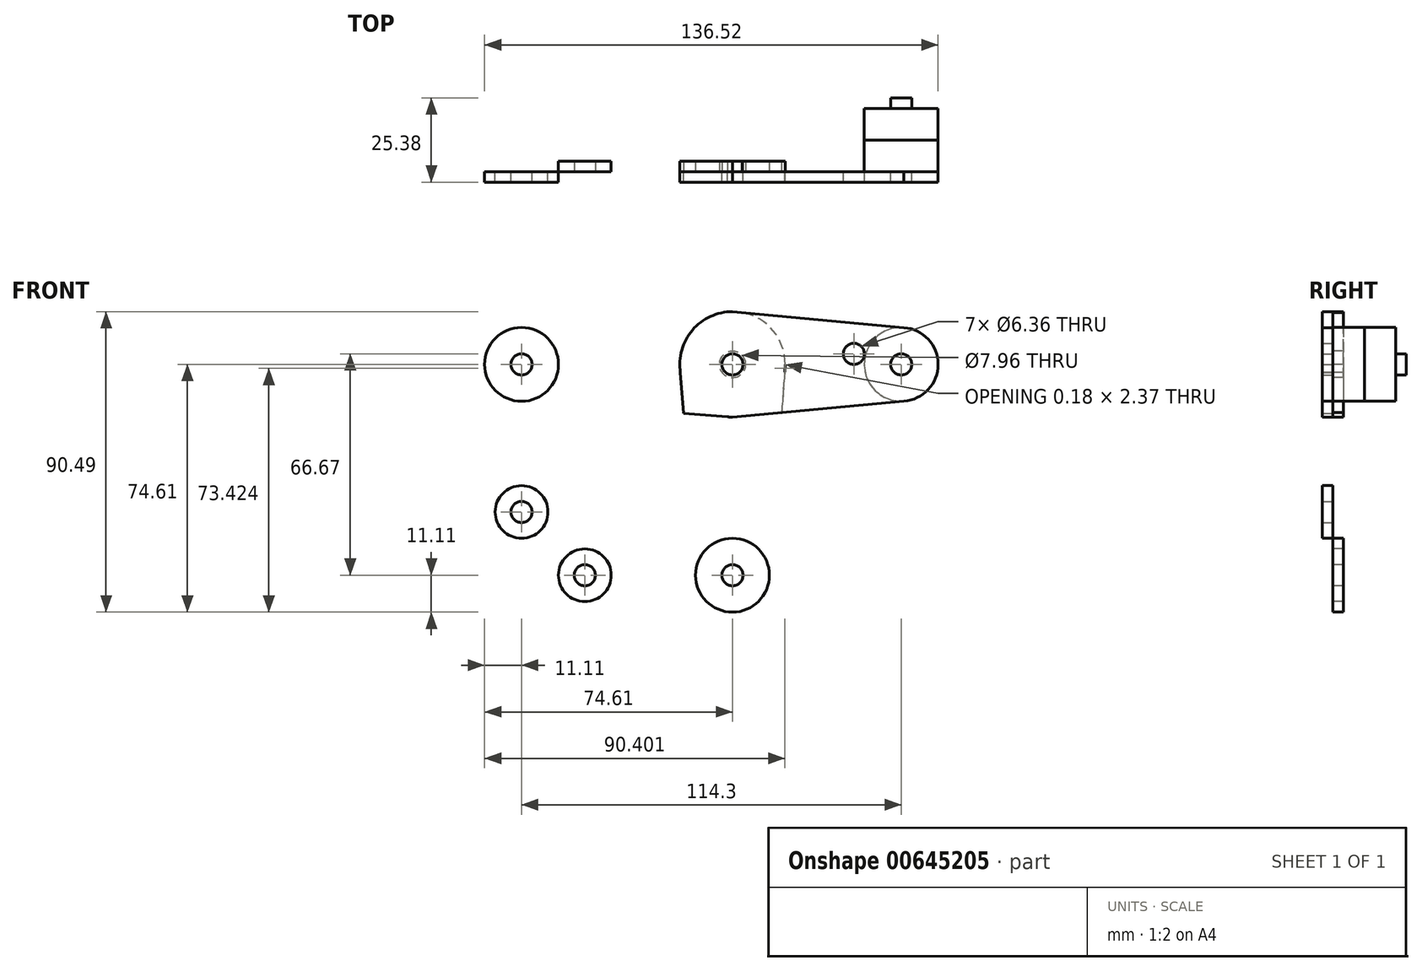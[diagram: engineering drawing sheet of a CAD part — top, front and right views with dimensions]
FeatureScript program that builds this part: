
annotation { "Feature Type Name" : "Feature", "Feature Type Description" : "" }
export const myFeature = defineFeature(function(context is Context, id is Id, definition is map)
    precondition{}
    {
        {
            var Q0;
            Q0=qCreatedBy(makeId("Front.planeOp"),FACE);
            var sketch = newSketch(context, id + "F0", { "sketchPlane" : qUnion([Q0])});
            skCircle(sketch, "E0", {"center": v(0, 0) * mm, "radius": 3.98 * mm});
            skCircle(sketch, "E1", {"center": v(0, 0) * mm, "radius": 15.88 * mm});
            skCircle(sketch, "E2", {"center": v(50.8, 0) * mm, "radius": 11.11 * mm});
            skCircle(sketch, "E3", {"center": v(50.8, 0) * mm, "radius": 3.18 * mm});
            skLineSegment(sketch, "E4", {"start": v(0, -15.88) * mm, "end": v(51.83, -11.06) * mm});
            skLineSegment(sketch, "E5", {"start": v(0, 15.88) * mm, "end": v(51.83, 11.06) * mm});
            skCircle(sketch, "E6", {"center": v(36.53, 3.17) * mm, "radius": 3.18 * mm});
            skLineSegment(sketch, "E7", {"start": v(0, 0) * mm, "end": v(50.8, 0) * mm, "construction": true});
            skCircle(sketch, "E8", {"center": v(-63.5, 0) * mm, "radius": 11.11 * mm});
            skLineSegment(sketch, "E9", {"start": v(-63.5, 0) * mm, "end": v(0, 0) * mm, "construction": true});
            skCircle(sketch, "E10", {"center": v(-63.5, 0) * mm, "radius": 3.18 * mm});
            skCircle(sketch, "E11", {"center": v(-63.5, -44.45) * mm, "radius": 7.94 * mm});
            skCircle(sketch, "E12", {"center": v(-63.5, -44.45) * mm, "radius": 3.18 * mm});
            skLineSegment(sketch, "E13", {"start": v(-63.5, 0) * mm, "end": v(-63.5, -44.45) * mm, "construction": true});
            skCircle(sketch, "E14", {"center": v(0, -63.5) * mm, "radius": 3.18 * mm});
            skCircle(sketch, "E15", {"center": v(0, -63.5) * mm, "radius": 11.11 * mm});
            skCircle(sketch, "E16", {"center": v(0, -42.85) * mm, "radius": 3.18 * mm});
            skLineSegment(sketch, "E17", {"start": v(0, 0) * mm, "end": v(0, -63.5) * mm, "construction": true});
            skCircle(sketch, "E18", {"center": v(-44.45, -63.5) * mm, "radius": 7.94 * mm});
            skLineSegment(sketch, "E19", {"start": v(0, -63.5) * mm, "end": v(-44.45, -63.5) * mm, "construction": true});
            skCircle(sketch, "E20", {"center": v(-44.45, -63.5) * mm, "radius": 3.18 * mm});
            skLineSegment(sketch, "E21", {"start": v(-63.5, -44.45) * mm, "end": v(-44.45, -63.5) * mm, "construction": true});
            skLineSegment(sketch, "E22", {"start": v(-44.45, -71.44) * mm, "end": v(0, -74.64) * mm});
            skLineSegment(sketch, "E23", {"start": v(-15.87, 0) * mm, "end": v(-12.5, -45.27) * mm});
            skLineSegment(sketch, "E24", {"start": v(-44.45, -55.56) * mm, "end": v(-19.86, -53.8) * mm});
            skPoint(sketch, "E25.newPointB", {"position": v(0, -52.36) * mm});
            skArc(sketch, "E25.filletArc", {"start": v(-19.86, -53.8) * mm, "mid": v(-14.41, -51.06) * mm, "end": v(-12.5, -45.27) * mm});
            skLineSegment(sketch, "E26", {"start": v(15.88, 0) * mm, "end": v(11.11, -63.5) * mm});
            skCircle(sketch, "E27", {"center": v(0, 0) * mm, "radius": 3.18 * mm});
            skLineSegment(sketch, "E28", {"start": v(-64.33, 11.08) * mm, "end": v(-1.2, 15.83) * mm});
            skLineSegment(sketch, "E29", {"start": v(-74.58, -0.8) * mm, "end": v(-71.42, -45.02) * mm});
            skLineSegment(sketch, "E30", {"start": v(-53.78, -19.88) * mm, "end": v(-55.58, -45.02) * mm});
            skLineSegment(sketch, "E31", {"start": v(-45.26, -12.52) * mm, "end": v(-1.2, -15.83) * mm});
            skPoint(sketch, "E32.newPointB", {"position": v(-52.36, 0) * mm});
            skArc(sketch, "E32.filletArc", {"start": v(-45.26, -12.52) * mm, "mid": v(-51.05, -14.43) * mm, "end": v(-53.78, -19.88) * mm});
            skSolve(sketch);
        }
        {
            var Q0;
            {var subQ0=sQuery(id+"F0.wireOp",EDGE,"E28");Q0=makeQuery(id+"F0.imprint","IMPRINT",FACE,{"disambiguationData":[TD([[makeQuery(id+"F0.imprint","IMPRINT",EDGE,{"derivedFrom":subQ0}),-1.0]])]});}
            var Q1;
            Q1=makeQuery(id+"F0.imprint","IMPRINT",FACE,{"disambiguationData":[TD([[makeQuery(id+"F0.imprint","IMPRINT",EDGE,{"derivedFrom":sQuery(id+"F0.wireOp",EDGE,"E6")}),-1.0]])]});
            var Q2;
            Q2=makeQuery(id+"F0.imprint","IMPRINT",FACE,{"disambiguationData":[TD([[makeQuery(id+"F0.imprint","IMPRINT",EDGE,{"derivedFrom":sQuery(id+"F0.wireOp",EDGE,"E0")}),-1.0]])]});
            var Q3;
            {var subQ0=sQuery(id+"F0.wireOp",EDGE,"E31");var subQ1=sQuery(id+"F0.wireOp",EDGE,"E1");var subQ2=makeQuery(id+"F0.imprint","INTERSECT",VERTEX,{"derivedFrom":[subQ1,subQ0]});Q3=makeQuery(id+"F0.imprint","IMPRINT",FACE,{"disambiguationData":[TD([[makeQuery(id+"F0.imprint","IMPRINT",EDGE,{"disambiguationData":[TD([[subQ2,1.0]])],"derivedFrom":subQ1}),-1.0]])]});}
            var Q4;
            {var subQ0=sQuery(id+"F0.wireOp",EDGE,"E4");var subQ1=sQuery(id+"F0.wireOp",EDGE,"E1");var subQ2=makeQuery(id+"F0.imprint","INTERSECT",VERTEX,{"disambiguationData":[OD(1.0)],"derivedFrom":[subQ1,subQ0]});Q4=makeQuery(id+"F0.imprint","IMPRINT",FACE,{"disambiguationData":[TD([[makeQuery(id+"F0.imprint","IMPRINT",EDGE,{"disambiguationData":[TD([[subQ2,-1.0]])],"derivedFrom":subQ1}),-1.0]])]});}
            var Q5;
            Q5=makeQuery(id+"F0.imprint","IMPRINT",FACE,{"disambiguationData":[TD([[makeQuery(id+"F0.imprint","IMPRINT",EDGE,{"derivedFrom":sQuery(id+"F0.wireOp",EDGE,"E3")}),-1.0]])]});
            var Q6;
            Q6=makeQuery(id+"F0.imprint","IMPRINT",FACE,{"disambiguationData":[TD([[makeQuery(id+"F0.imprint","IMPRINT",EDGE,{"derivedFrom":sQuery(id+"F0.wireOp",EDGE,"E10")}),-1.0]])]});
            var Q7;
            Q7=makeQuery(id+"F0.imprint","IMPRINT",FACE,{"disambiguationData":[TD([[makeQuery(id+"F0.imprint","IMPRINT",EDGE,{"derivedFrom":sQuery(id+"F0.wireOp",EDGE,"E12")}),-1.0]])]});
            var Q8;
            Q8=makeQuery(id+"F0.imprint","IMPRINT",FACE,{"disambiguationData":[TD([[makeQuery(id+"F0.imprint","IMPRINT",EDGE,{"derivedFrom":sQuery(id+"F0.wireOp",EDGE,"E0")}),1.0]])]});
            extrude(context, id + "F1", {"entities" : qUnion([Q0, Q1, Q2, Q3, Q4, Q5, Q6, Q7, Q8]), "depth" : 3.17 * mm, "offsetDistance" : 25.4 * mm});
        }
        {
            var Q0;
            {var subQ0=sQuery(id+"F0.wireOp",EDGE,"E31");var subQ1=sQuery(id+"F0.wireOp",EDGE,"E1");var subQ2=makeQuery(id+"F0.imprint","INTERSECT",VERTEX,{"derivedFrom":[subQ1,subQ0]});Q0=makeQuery(id+"F0.imprint","IMPRINT",FACE,{"disambiguationData":[TD([[makeQuery(id+"F0.imprint","IMPRINT",EDGE,{"disambiguationData":[TD([[subQ2,1.0]])],"derivedFrom":subQ1}),-1.0]])]});}
            var Q1;
            {var subQ0=sQuery(id+"F0.wireOp",EDGE,"E4");var subQ1=sQuery(id+"F0.wireOp",EDGE,"E1");var subQ2=makeQuery(id+"F0.imprint","INTERSECT",VERTEX,{"disambiguationData":[OD(1.0)],"derivedFrom":[subQ1,subQ0]});Q1=makeQuery(id+"F0.imprint","IMPRINT",FACE,{"disambiguationData":[TD([[makeQuery(id+"F0.imprint","IMPRINT",EDGE,{"disambiguationData":[TD([[subQ2,-1.0]])],"derivedFrom":subQ1}),-1.0]])]});}
            var Q2;
            Q2=makeQuery(id+"F0.imprint","IMPRINT",FACE,{"disambiguationData":[TD([[makeQuery(id+"F0.imprint","IMPRINT",EDGE,{"derivedFrom":sQuery(id+"F0.wireOp",EDGE,"E0")}),-1.0]])]});
            var Q3;
            Q3=makeQuery(id+"F0.imprint","IMPRINT",FACE,{"disambiguationData":[TD([[makeQuery(id+"F0.imprint","IMPRINT",EDGE,{"derivedFrom":sQuery(id+"F0.wireOp",EDGE,"E16")}),-1.0]])]});
            var Q4;
            Q4=makeQuery(id+"F0.imprint","IMPRINT",FACE,{"disambiguationData":[TD([[makeQuery(id+"F0.imprint","IMPRINT",EDGE,{"derivedFrom":sQuery(id+"F0.wireOp",EDGE,"E14")}),-1.0]])]});
            var Q5;
            Q5=makeQuery(id+"F0.imprint","IMPRINT",FACE,{"disambiguationData":[TD([[makeQuery(id+"F0.imprint","IMPRINT",EDGE,{"derivedFrom":sQuery(id+"F0.wireOp",EDGE,"E20")}),-1.0]])]});
            extrude(context, id + "F2", {"entities" : qUnion([Q0, Q1, Q2, Q3, Q4, Q5]), "oppositeDirection" : true, "depth" : 3.17 * mm, "offsetDistance" : 25.4 * mm});
        }
        {
            var Q0;
            Q0=makeQuery(id+"F1.opExtrude","CAP_FACE",FACE,{"disambiguationData":[OSD([sQuery(id+"F0.wireOp",EDGE,"E0"),sQuery(id+"F0.wireOp",EDGE,"E1"),sQuery(id+"F0.wireOp",EDGE,"E2"),sQuery(id+"F0.wireOp",EDGE,"E3"),sQuery(id+"F0.wireOp",EDGE,"E4"),sQuery(id+"F0.wireOp",EDGE,"E5"),sQuery(id+"F0.wireOp",EDGE,"E6"),sQuery(id+"F0.wireOp",EDGE,"E8"),sQuery(id+"F0.wireOp",EDGE,"E10"),sQuery(id+"F0.wireOp",EDGE,"E11"),sQuery(id+"F0.wireOp",EDGE,"E12"),sQuery(id+"F0.wireOp",EDGE,"E23"),sQuery(id+"F0.wireOp",EDGE,"E26"),sQuery(id+"F0.wireOp",EDGE,"E28"),sQuery(id+"F0.wireOp",EDGE,"E29"),sQuery(id+"F0.wireOp",EDGE,"E30"),sQuery(id+"F0.wireOp",EDGE,"E31"),sQuery(id+"F0.wireOp",EDGE,"E32.filletArc")])],"isStart":false});
            var sketch = newSketch(context, id + "F3", { "sketchPlane" : qUnion([Q0])});
            skCircle(sketch, "E33", {"center": v(-63.5, 0) * mm, "radius": 3.98 * mm});
            skCircle(sketch, "E34", {"center": v(0, 0) * mm, "radius": 3.98 * mm});
            skCircle(sketch, "E35.0", {"center": v(50.8, 0) * mm, "radius": 11.11 * mm});
            skSolve(sketch);
        }
        {
            var Q0;
            Q0=makeQuery(id+"F0.imprint","IMPRINT",FACE,{"disambiguationData":[TD([[makeQuery(id+"F0.imprint","IMPRINT",EDGE,{"derivedFrom":sQuery(id+"F0.wireOp",EDGE,"E16")}),-1.0]])]});
            var sketch = newSketch(context, id + "F4", { "sketchPlane" : qUnion([Q0])});
            skArc(sketch, "E36.0.0", {"start": v(-0.8, -74.58) * mm, "mid": v(7.57, -71.64) * mm, "end": v(11.11, -63.5) * mm});
            skArc(sketch, "E36.0.1", {"start": v(11.11, -63.5) * mm, "mid": v(-7.57, -55.36) * mm, "end": v(-0.8, -74.58) * mm});
            skPoint(sketch, "E37.0", {"position": v(-44.45, -63.5) * mm});
            skCircle(sketch, "E38", {"center": v(-44.45, -63.5) * mm, "radius": 3.98 * mm});
            skLineSegment(sketch, "E39", {"start": v(51.18, 0) * mm, "end": v(6.29, -62.6) * mm, "construction": true});
            skLineSegment(sketch, "E40", {"start": v(5, -53.58) * mm, "end": v(7.57, -71.64) * mm});
            skSolve(sketch);
        }
        {
            var Q0;
            Q0=qCreatedBy(makeId("Front.planeOp"),FACE);
            cPlane(context, id + "F5", {"entities" : qUnion([Q0]), "cplaneType" : CPlaneType.OFFSET, "offset" : 9.52 * mm, "oppositeDirection" : true, "width" : 152.4 * mm, "height" : 152.4 * mm});
        }
        {
            var Q0;
            Q0=makeQuery(id+"F3.imprint","IMPRINT",FACE,{"disambiguationData":[TD([[makeQuery(id+"F3.imprint","IMPRINT",EDGE,{"derivedFrom":makeQuery(id+"F1.opExtrude","CAP_EDGE",EDGE,{"disambiguationData":[OSD([sQuery(id+"F0.wireOp",EDGE,"E3")])],"isStart":false})}),-1.0]])]});
            var Q1;
            {var subQ4=sQuery(id+"F4.wireOp",EDGE,"E40");Q1=makeQuery(id+"F4.imprint","IMPRINT",FACE,{"disambiguationData":[TD([[makeQuery(id+"F4.imprint","IMPRINT",EDGE,{"derivedFrom":subQ4}),-1.0]])]});}
            var Q2;
            Q2=makeQuery(id+"F3.imprint","IMPRINT",FACE,{"disambiguationData":[TD([[makeQuery(id+"F3.imprint","IMPRINT",EDGE,{"derivedFrom":makeQuery(id+"F1.opExtrude","CAP_EDGE",EDGE,{"disambiguationData":[OSD([sQuery(id+"F0.wireOp",EDGE,"E12")])],"isStart":false})}),1.0]])]});
            var Q3;
            Q3=makeQuery(id+"F3.imprint","IMPRINT",FACE,{"disambiguationData":[TD([[makeQuery(id+"F3.imprint","IMPRINT",EDGE,{"derivedFrom":makeQuery(id+"F1.opExtrude","CAP_EDGE",EDGE,{"disambiguationData":[OSD([sQuery(id+"F0.wireOp",EDGE,"E10")])],"isStart":false})}),1.0]])]});
            var Q4;
            Q4=makeQuery(id+"F3.imprint","IMPRINT",FACE,{"disambiguationData":[TD([[makeQuery(id+"F3.imprint","IMPRINT",EDGE,{"derivedFrom":makeQuery(id+"F1.opExtrude","CAP_EDGE",EDGE,{"disambiguationData":[OSD([sQuery(id+"F0.wireOp",EDGE,"E3")])],"isStart":false})}),1.0]])]});
            var Q5;
            Q5=qCreatedBy(id+"F5.planeOp",FACE);
            extrude(context, id + "F6", {"entities" : qUnion([Q0, Q1, Q2, Q3, Q4]), "endBound" : BoundingType.UP_TO_SURFACE, "oppositeDirection" : true, "depth" : 11.68 * mm, "endBoundEntityFace" : qUnion([Q5]), "offsetDistance" : 25.4 * mm});
        }
        {
            var Q0;
            Q0=makeQuery(id+"F2.opExtrude","SWEPT_BODY",BODY,{"disambiguationData":[OSD([sQuery(id+"F0.wireOp",EDGE,"E0"),sQuery(id+"F0.wireOp",EDGE,"E1"),sQuery(id+"F0.wireOp",EDGE,"E4"),sQuery(id+"F0.wireOp",EDGE,"E5"),sQuery(id+"F0.wireOp",EDGE,"E14"),sQuery(id+"F0.wireOp",EDGE,"E15"),sQuery(id+"F0.wireOp",EDGE,"E16"),sQuery(id+"F0.wireOp",EDGE,"E18"),sQuery(id+"F0.wireOp",EDGE,"E20"),sQuery(id+"F0.wireOp",EDGE,"E22"),sQuery(id+"F0.wireOp",EDGE,"E23"),sQuery(id+"F0.wireOp",EDGE,"E24"),sQuery(id+"F0.wireOp",EDGE,"E25.filletArc"),sQuery(id+"F0.wireOp",EDGE,"E26")])]});
            var Q1;
            Q1=makeQuery(id+"F1.opExtrude","SWEPT_BODY",BODY,{"disambiguationData":[OSD([sQuery(id+"F0.wireOp",EDGE,"E1"),sQuery(id+"F0.wireOp",EDGE,"E2"),sQuery(id+"F0.wireOp",EDGE,"E3"),sQuery(id+"F0.wireOp",EDGE,"E4"),sQuery(id+"F0.wireOp",EDGE,"E5"),sQuery(id+"F0.wireOp",EDGE,"E6"),sQuery(id+"F0.wireOp",EDGE,"E8"),sQuery(id+"F0.wireOp",EDGE,"E10"),sQuery(id+"F0.wireOp",EDGE,"E11"),sQuery(id+"F0.wireOp",EDGE,"E12"),sQuery(id+"F0.wireOp",EDGE,"E23"),sQuery(id+"F0.wireOp",EDGE,"E26"),sQuery(id+"F0.wireOp",EDGE,"E27"),sQuery(id+"F0.wireOp",EDGE,"E28"),sQuery(id+"F0.wireOp",EDGE,"E29"),sQuery(id+"F0.wireOp",EDGE,"E30"),sQuery(id+"F0.wireOp",EDGE,"E31"),sQuery(id+"F0.wireOp",EDGE,"E32.filletArc")])]});
            var Q2;
            Q2=makeQuery(id+"F6.opExtrude","SWEPT_BODY",BODY,{"disambiguationData":[OSD([sQuery(id+"F4.wireOp",EDGE,"E36.0.0"),sQuery(id+"F4.wireOp",EDGE,"E36.0.1"),sQuery(id+"F4.wireOp",EDGE,"E40")])]});
            var Q3;
            Q3=makeQuery(id+"F6.opExtrude","SWEPT_BODY",BODY,{"disambiguationData":[OSD([sQuery(id+"F3.wireOp",EDGE,"E35.0")])]});
            var Q4;
            Q4=makeQuery(id+"F6.opExtrude","SWEPT_BODY",BODY,{"disambiguationData":[OSD([sQuery(id+"F0.wireOp",EDGE,"E12")])]});
            var Q5;
            Q5=makeQuery(id+"F6.opExtrude","SWEPT_BODY",BODY,{"disambiguationData":[OSD([sQuery(id+"F0.wireOp",EDGE,"E10")])]});
            booleanBodies(context, id + "F7", {"operationType" : BooleanOperationType.SUBTRACTION, "tools" : qUnion([Q0, Q1]), "targets" : qUnion([Q2, Q3, Q4, Q5]), "keepTools" : true});
        }
        {
            var Q0;
            Q0=makeQuery(id+"F6.opExtrude","SWEPT_BODY",BODY,{"disambiguationData":[OSD([sQuery(id+"F0.wireOp",EDGE,"E10")])]});
            var Q1;
            Q1=makeQuery(id+"F6.opExtrude","SWEPT_BODY",BODY,{"disambiguationData":[OSD([sQuery(id+"F0.wireOp",EDGE,"E12")])]});
            var Q2;
            Q2=makeQuery(id+"F6.opExtrude","SWEPT_BODY",BODY,{"disambiguationData":[OSD([sQuery(id+"F3.wireOp",EDGE,"E35.0")])]});
            var Q3;
            Q3=makeQuery(id+"F6.opExtrude","SWEPT_BODY",BODY,{"disambiguationData":[OSD([sQuery(id+"F4.wireOp",EDGE,"E36.0.0"),sQuery(id+"F4.wireOp",EDGE,"E36.0.1"),sQuery(id+"F4.wireOp",EDGE,"E40")])]});
            var Q4;
            Q4=qCreatedBy(id+"F5.planeOp",FACE);
            mirror(context, id + "F8", {"entities" : qUnion([Q0, Q1, Q2, Q3]), "mirrorPlane" : qUnion([Q4])});
        }
    });
